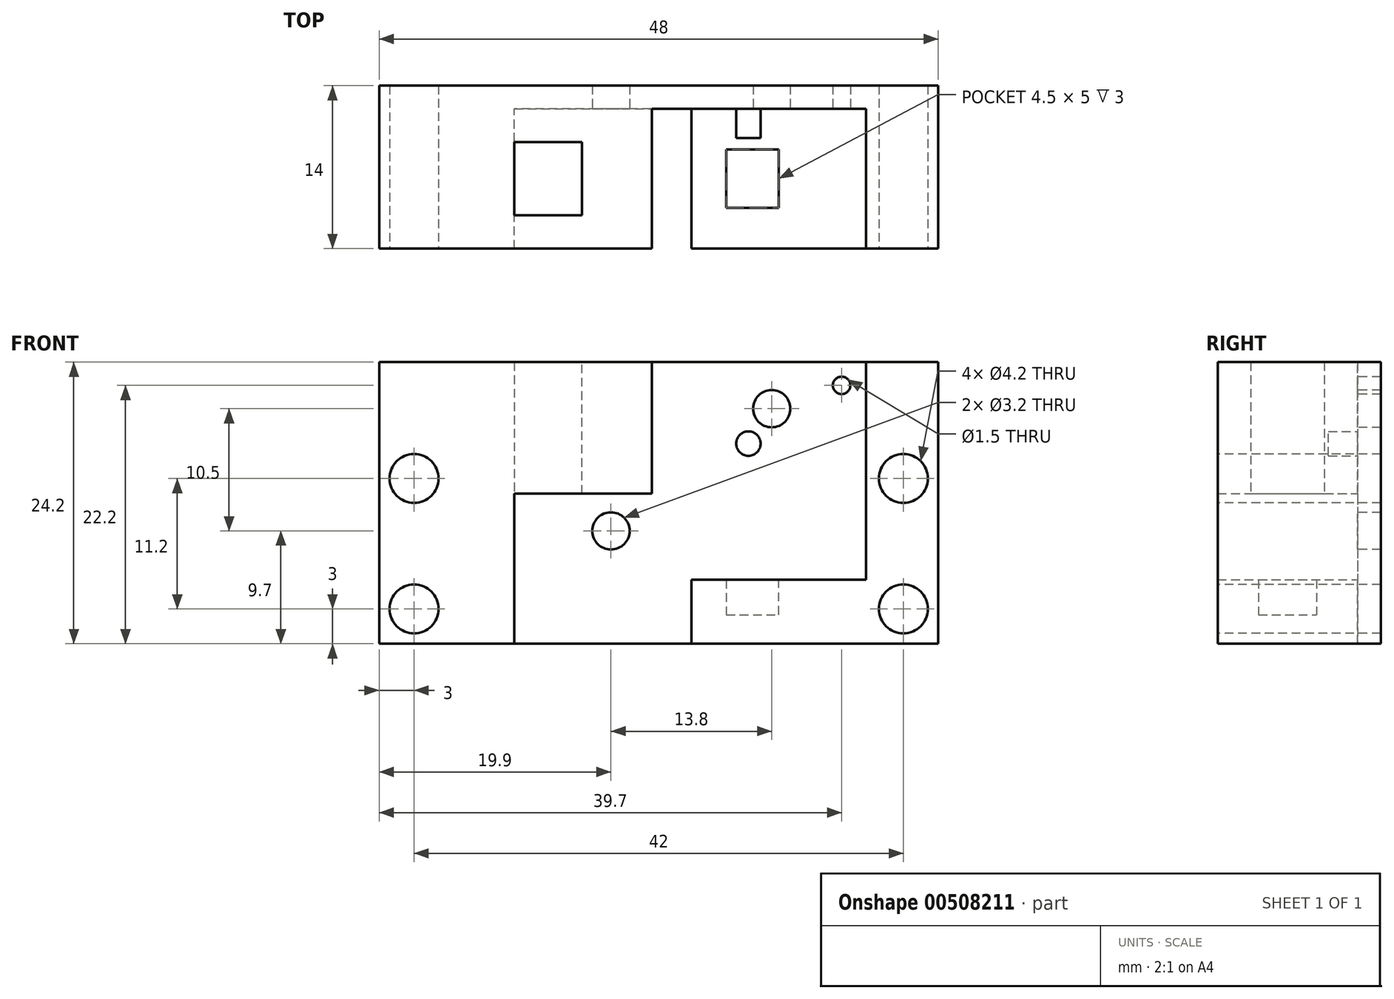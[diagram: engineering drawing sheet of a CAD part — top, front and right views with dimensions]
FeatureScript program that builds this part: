
annotation { "Feature Type Name" : "Feature", "Feature Type Description" : "" }
export const myFeature = defineFeature(function(context is Context, id is Id, definition is map)
    precondition{}
    {
        {
            var Q0;
            Q0=qCreatedBy(makeId("Front.planeOp"),FACE);
            var sketch = newSketch(context, id + "F0", { "sketchPlane" : qUnion([Q0])});
            skLineSegment(sketch, "E0.bottom", {"start": v(-24, 12.1) * mm, "end": v(24, 12.1) * mm});
            skLineSegment(sketch, "E0.top", {"start": v(-24, -12.1) * mm, "end": v(24, -12.1) * mm});
            skLineSegment(sketch, "E0.left", {"start": v(-24, 12.1) * mm, "end": v(-24, -12.1) * mm});
            skLineSegment(sketch, "E0.right", {"start": v(24, 12.1) * mm, "end": v(24, -12.1) * mm});
            skPoint(sketch, "E0.middle", {"position": v(0, 0) * mm});
            skLineSegment(sketch, "E1", {"start": v(-12.4, 12.1) * mm, "end": v(-12.4, -12.1) * mm});
            skLineSegment(sketch, "E2", {"start": v(-12.4, 0.8) * mm, "end": v(-0.6, 0.8) * mm});
            skLineSegment(sketch, "E3", {"start": v(-0.6, 0.8) * mm, "end": v(-0.6, 12.1) * mm});
            skLineSegment(sketch, "E4", {"start": v(-6.6, 0.8) * mm, "end": v(-6.6, 12.1) * mm});
            skLineSegment(sketch, "E5", {"start": v(17.8, 12.1) * mm, "end": v(17.8, -12.1) * mm});
            skLineSegment(sketch, "E6", {"start": v(2.8, -12.1) * mm, "end": v(2.8, -6.6) * mm});
            skLineSegment(sketch, "E7", {"start": v(2.8, -6.6) * mm, "end": v(17.8, -6.6) * mm});
            skLineSegment(sketch, "E8", {"start": v(5.8, -6.6) * mm, "end": v(5.8, -9.6) * mm});
            skLineSegment(sketch, "E9", {"start": v(5.8, -9.6) * mm, "end": v(10.3, -9.6) * mm});
            skLineSegment(sketch, "E10", {"start": v(10.3, -9.6) * mm, "end": v(10.3, -6.6) * mm});
            skSolve(sketch);
        }
        {
            var Q0;
            Q0=qCreatedBy(makeId("Front.planeOp"),FACE);
            cPlane(context, id + "F1", {"entities" : qUnion([Q0]), "cplaneType" : CPlaneType.OFFSET, "offset" : 6 * mm, "oppositeDirection" : true, "width" : 150 * mm, "height" : 150 * mm});
        }
        {
            var Q0;
            Q0=qCreatedBy(id+"F1.planeOp",FACE);
            var sketch = newSketch(context, id + "F2", { "sketchPlane" : qUnion([Q0])});
            skLineSegment(sketch, "E11.bottom", {"start": v(24, -12.1) * mm, "end": v(-24, -12.1) * mm});
            skLineSegment(sketch, "E11.top", {"start": v(24, 12.1) * mm, "end": v(-24, 12.1) * mm});
            skLineSegment(sketch, "E11.left", {"start": v(24, -12.1) * mm, "end": v(24, 12.1) * mm});
            skLineSegment(sketch, "E11.right", {"start": v(-24, -12.1) * mm, "end": v(-24, 12.1) * mm});
            skPoint(sketch, "E11.middle", {"position": v(0, 0) * mm});
            skCircle(sketch, "E12", {"center": v(9.7, 8.1) * mm, "radius": 1.6 * mm});
            skCircle(sketch, "E13", {"center": v(-4.1, -2.4) * mm, "radius": 1.6 * mm});
            skCircle(sketch, "E14", {"center": v(-21, 2.1) * mm, "radius": 2.1 * mm});
            skCircle(sketch, "E15", {"center": v(-21, -9.1) * mm, "radius": 2.1 * mm});
            skCircle(sketch, "E16", {"center": v(21, -9.1) * mm, "radius": 2.1 * mm});
            skCircle(sketch, "E17", {"center": v(21, 2.1) * mm, "radius": 2.1 * mm});
            skCircle(sketch, "E18", {"center": v(15.7, 10.1) * mm, "radius": 0.75 * mm});
            skCircle(sketch, "E19", {"center": v(7.7, 5.1) * mm, "radius": 1.05 * mm});
            skSolve(sketch);
        }
        {
            var Q0;
            Q0=makeQuery(id+"F2.imprint","IMPRINT",FACE,{"disambiguationData":[TD([[makeQuery(id+"F2.imprint","IMPRINT",EDGE,{"derivedFrom":sQuery(id+"F2.wireOp",EDGE,"E11.bottom")}),-1.0]])]});
            extrude(context, id + "F3", {"entities" : qUnion([Q0]), "oppositeDirection" : true, "depth" : 2 * mm, "offsetDistance" : 25 * mm});
        }
        {
            var Q0;
            {var subQ0=sQuery(id+"F0.wireOp",EDGE,"E0.left");Q0=makeQuery(id+"F0.imprint","IMPRINT",FACE,{"disambiguationData":[TD([[makeQuery(id+"F0.imprint","IMPRINT",EDGE,{"derivedFrom":subQ0}),1.0]])]});}
            var Q1;
            {var subQ0=sQuery(id+"F0.wireOp",EDGE,"E4");Q1=makeQuery(id+"F0.imprint","IMPRINT",FACE,{"disambiguationData":[TD([[makeQuery(id+"F0.imprint","IMPRINT",EDGE,{"derivedFrom":subQ0}),1.0]])]});}
            var Q2;
            {var subQ0=sQuery(id+"F0.wireOp",EDGE,"E3");Q2=makeQuery(id+"F0.imprint","IMPRINT",FACE,{"disambiguationData":[TD([[makeQuery(id+"F0.imprint","IMPRINT",EDGE,{"derivedFrom":subQ0}),1.0]])]});}
            var Q3;
            {var subQ2=sQuery(id+"F0.wireOp",EDGE,"E8");Q3=makeQuery(id+"F0.imprint","IMPRINT",FACE,{"disambiguationData":[TD([[makeQuery(id+"F0.imprint","IMPRINT",EDGE,{"derivedFrom":subQ2}),1.0]])]});}
            var Q4;
            {var subQ4=sQuery(id+"F0.wireOp",EDGE,"E6");Q4=makeQuery(id+"F0.imprint","IMPRINT",FACE,{"disambiguationData":[TD([[makeQuery(id+"F0.imprint","IMPRINT",EDGE,{"derivedFrom":subQ4}),-1.0]])]});}
            var Q5;
            {var subQ0=sQuery(id+"F0.wireOp",EDGE,"E0.right");Q5=makeQuery(id+"F0.imprint","IMPRINT",FACE,{"disambiguationData":[TD([[makeQuery(id+"F0.imprint","IMPRINT",EDGE,{"derivedFrom":subQ0}),-1.0]])]});}
            extrude(context, id + "F4", {"entities" : qUnion([Q0, Q1, Q2, Q3, Q4, Q5]), "operationType" : NewBodyOperationType.ADD, "depth" : 12 * mm, "offsetDistance" : 25 * mm, "symmetric" : true});
        }
        {
            var Q0;
            {var subQ0=sQuery(id+"F0.wireOp",EDGE,"E4");Q0=makeQuery(id+"F0.imprint","IMPRINT",FACE,{"disambiguationData":[TD([[makeQuery(id+"F0.imprint","IMPRINT",EDGE,{"derivedFrom":subQ0}),1.0]])]});}
            extrude(context, id + "F5", {"entities" : qUnion([Q0]), "operationType" : NewBodyOperationType.REMOVE, "depth" : 6.3 * mm, "offsetDistance" : 25 * mm, "symmetric" : true});
        }
        {
            var Q0;
            {var subQ2=sQuery(id+"F0.wireOp",EDGE,"E8");Q0=makeQuery(id+"F0.imprint","IMPRINT",FACE,{"disambiguationData":[TD([[makeQuery(id+"F0.imprint","IMPRINT",EDGE,{"derivedFrom":subQ2}),1.0]])]});}
            extrude(context, id + "F6", {"entities" : qUnion([Q0]), "operationType" : NewBodyOperationType.REMOVE, "depth" : 5 * mm, "offsetDistance" : 25 * mm, "symmetric" : true});
        }
        {
            var Q0;
            Q0=makeQuery(id+"F2.imprint","IMPRINT",FACE,{"disambiguationData":[TD([[makeQuery(id+"F2.imprint","IMPRINT",EDGE,{"derivedFrom":sQuery(id+"F2.wireOp",EDGE,"E16")}),1.0]])]});
            var Q1;
            Q1=makeQuery(id+"F2.imprint","IMPRINT",FACE,{"disambiguationData":[TD([[makeQuery(id+"F2.imprint","IMPRINT",EDGE,{"derivedFrom":sQuery(id+"F2.wireOp",EDGE,"E17")}),1.0]])]});
            var Q2;
            Q2=makeQuery(id+"F2.imprint","IMPRINT",FACE,{"disambiguationData":[TD([[makeQuery(id+"F2.imprint","IMPRINT",EDGE,{"derivedFrom":sQuery(id+"F2.wireOp",EDGE,"E14")}),1.0]])]});
            var Q3;
            Q3=makeQuery(id+"F2.imprint","IMPRINT",FACE,{"disambiguationData":[TD([[makeQuery(id+"F2.imprint","IMPRINT",EDGE,{"derivedFrom":sQuery(id+"F2.wireOp",EDGE,"E15")}),1.0]])]});
            extrude(context, id + "F7", {"entities" : qUnion([Q0, Q1, Q2, Q3]), "operationType" : NewBodyOperationType.REMOVE, "endBound" : BoundingType.THROUGH_ALL, "oppositeDirection" : true, "depth" : 25 * mm, "offsetDistance" : 25 * mm, "hasSecondDirection" : true, "secondDirectionBound" : BoundingType.THROUGH_ALL, "secondDirectionOppositeDirection" : false, "secondDirectionDepth" : 25 * mm});
        }
        {
            var Q0;
            Q0=makeQuery(id+"F2.imprint","IMPRINT",FACE,{"disambiguationData":[TD([[makeQuery(id+"F2.imprint","IMPRINT",EDGE,{"derivedFrom":sQuery(id+"F2.wireOp",EDGE,"E19")}),1.0]])]});
            var Q1;
            Q1=makeQuery(id+"F3.opExtrude","CAP_FACE",FACE,{"disambiguationData":[OSD([sQuery(id+"F2.wireOp",EDGE,"E11.bottom"),sQuery(id+"F2.wireOp",EDGE,"E11.top"),sQuery(id+"F2.wireOp",EDGE,"E11.left"),sQuery(id+"F2.wireOp",EDGE,"E11.right"),sQuery(id+"F2.wireOp",EDGE,"E12"),sQuery(id+"F2.wireOp",EDGE,"E13"),sQuery(id+"F2.wireOp",EDGE,"E14"),sQuery(id+"F2.wireOp",EDGE,"E15"),sQuery(id+"F2.wireOp",EDGE,"E16"),sQuery(id+"F2.wireOp",EDGE,"E17"),sQuery(id+"F2.wireOp",EDGE,"E18"),sQuery(id+"F2.wireOp",EDGE,"E19")])],"isStart":false});
            extrude(context, id + "F8", {"entities" : qUnion([Q0]), "operationType" : NewBodyOperationType.ADD, "depth" : 2.5 * mm, "offsetDistance" : 25 * mm, "hasSecondDirection" : true, "secondDirectionBound" : BoundingType.UP_TO_SURFACE, "secondDirectionOppositeDirection" : true, "secondDirectionDepth" : 25 * mm, "secondDirectionBoundEntityFace" : qUnion([Q1])});
        }
    });
